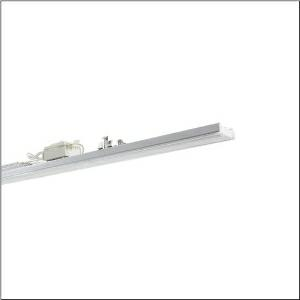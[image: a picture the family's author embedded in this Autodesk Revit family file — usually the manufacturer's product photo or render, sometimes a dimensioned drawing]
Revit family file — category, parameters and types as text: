
# Revit family: licross_r__11_recessed_mo_51te11dn4axg_54eb
name_source: partatom
category: Lighting Fixtures
units: mm (PartAtom-declared; Revit-internal decimal feet)

## family parameters
Cut with Voids When Loaded = No
Host = Face
Light Source = No
Part Type = Normal
Room Calculation Point = No
Round Connector Dimension = Use Diameter
Shared = No

## types (1)
- --- (1 x LED, 10080 lm, 56.7 W, 4000K)
    Apparent Load = 57 VA
    CIE Flux Codes = 89 96 99 100 100
    Color Rendering = 80
    Color Temperature = 4000K
    Default Elevation = 1800 mm
    Description = Licross® 11 Recessed MO, luminaire insert, of sheet steel, galvanised, coil coated, white, length: 1.500mm, width: 66mm, height: 67mm, LED rated luminous flux: 10.080lm, light colour: 840, control gear: DALI 2, with plug, 5-pole, with phase selection, mains connection: 220..240V, AC, 50/60Hz, rated input power: 57W, internal wiring halogen-free, primary light control with lens, of plastic, primary optical cover: cover, of PMMA, light emission: direct distribution, primary light characteristic: symmetric, protection rating (complete): IP54, insulation class (complete): insulation class I (protective earthing), certification: CE, ENEC, VDE, UKCA, protection symbol: D if used in an environment with non-conductive dust loads with corresponding accessories, impact resistance: IK06, permissible ambient temperature for indoor applications: -25..+35°C, corresponds to IFS (International Featured Standards) requirements for safety and quality in the food industry, reducing of maximum allowable ambient temperature of 5°C with ceiling mounting, LABS conformity tested according to VDMA 24364:2018-05, packaging unit: 1 piece
    Height = 58 mm
    Lamp = 1 x LED
    Lamp Light Flux = 10080 lm
    Lamp Power = 56.7 W
    Lamp count = 1
    Length = 1500 mm
    Luminous efficacy = 178 lm/W
    Manufacturer = Siteco
    ModVariant = No
    Model = 51TE11DN4AXG
    Mounting Place = Ceiling
    Mounting Type = Pendant
    Number of Poles = 1
    OnlyDefault = Yes
    Power Factor = 1
    Product Name = Licross® 11 Recessed MO
    Product group = luminaire insert | ceiling pendant
    ProductGroupID = 902
    Protection Class = Protection class I
    Protection Degree = IP 54
    RLX_Detail_Level = 1
    RLX_Emergency_Light_Flux = 0 lm
    RLX_Emergency_Type = 0
    RLX_Emergency_Type_DB = No
    RlxData = <blob elided: 24497 chars, md5=9a5ed374>
    Socket = socket
    Standby Power = 0 W
    System Light Flux = 10080 lm
    System Power = 57 W
    Type Comments = factory setting: luminous flux: 100 % | dim-lin: 254 | 378 mA
    Type Image = l_1296930.jpg
    URL = http://relux.com
    VarID = @adj_120087
    Voltage = 0 V
    Weight = 0.00 kg
    Width = 66 mm

## geometry (parser evidence)
native form markers: Blend x4, Sweep x10
no freeform markers — native parametric forms only
